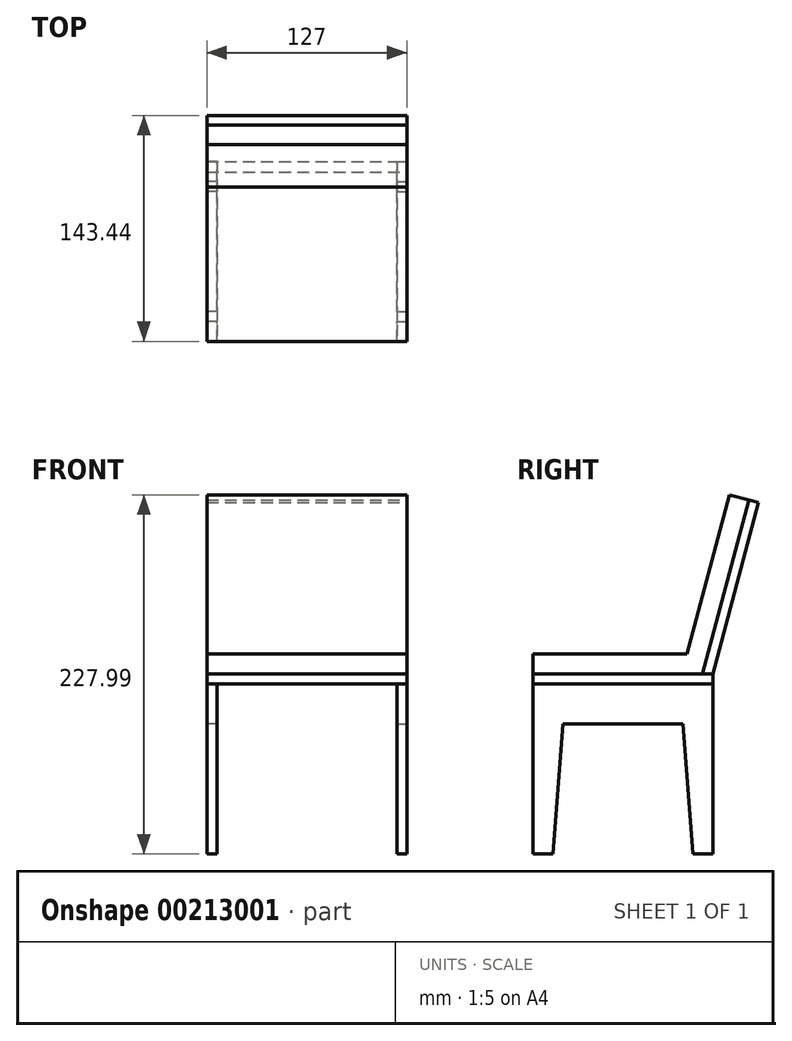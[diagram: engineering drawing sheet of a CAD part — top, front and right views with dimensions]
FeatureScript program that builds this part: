
annotation { "Feature Type Name" : "Feature", "Feature Type Description" : "" }
export const myFeature = defineFeature(function(context is Context, id is Id, definition is map)
    precondition{}
    {
        {
            var Q0;
            Q0=qCreatedBy(makeId("Top.planeOp"),FACE);
            cPlane(context, id + "F0", {"entities" : qUnion([Q0]), "cplaneType" : CPlaneType.OFFSET, "offset" : 114.3 * mm, "width" : 152.4 * mm, "height" : 152.4 * mm});
        }
        {
            var Q0;
            Q0=qCreatedBy(id+"F0.planeOp",FACE);
            var sketch = newSketch(context, id + "F1", { "sketchPlane" : qUnion([Q0])});
            skLineSegment(sketch, "E0.bottom", {"start": v(63.5, 57.15) * mm, "end": v(-63.5, 57.15) * mm});
            skLineSegment(sketch, "E0.top", {"start": v(63.5, -57.15) * mm, "end": v(-63.5, -57.15) * mm});
            skLineSegment(sketch, "E0.left", {"start": v(63.5, 57.15) * mm, "end": v(63.5, -57.15) * mm});
            skLineSegment(sketch, "E0.right", {"start": v(-63.5, 57.15) * mm, "end": v(-63.5, -57.15) * mm});
            skPoint(sketch, "E0.middle", {"position": v(0, 0) * mm});
            skSolve(sketch);
        }
        {
            var Q0;
            Q0=makeQuery(id+"F1.imprint","IMPRINT",FACE,{"disambiguationData":[TD([[makeQuery(id+"F1.imprint","IMPRINT",EDGE,{"derivedFrom":sQuery(id+"F1.wireOp",EDGE,"E0.bottom")}),1.0]])]});
            extrude(context, id + "F2", {"entities" : qUnion([Q0]), "oppositeDirection" : true, "depth" : 6.35 * mm});
        }
        {
            var Q0;
            Q0=makeQuery(id+"F2.opExtrude","SWEPT_FACE",FACE,{"disambiguationData":[OSD([sQuery(id+"F1.wireOp",EDGE,"E0.left")])]});
            var sketch = newSketch(context, id + "F3", { "sketchPlane" : qUnion([Q0])});
            skLineSegment(sketch, "E1", {"start": v(57.15, 114.3) * mm, "end": v(86.3, 223.06) * mm});
            skLineSegment(sketch, "E2", {"start": v(86.3, 223.06) * mm, "end": v(80.16, 224.7) * mm});
            skLineSegment(sketch, "E3", {"start": v(80.16, 224.7) * mm, "end": v(50.58, 114.3) * mm});
            skSolve(sketch);
        }
        {
            var Q0;
            {var subQ0=sQuery(id+"F3.wireOp",EDGE,"E1");Q0=makeQuery(id+"F3.imprint","IMPRINT",FACE,{"disambiguationData":[TD([[makeQuery(id+"F3.imprint","IMPRINT",EDGE,{"derivedFrom":subQ0}),1.0]])]});}
            var Q1;
            Q1=makeQuery(id+"F2.opExtrude","SWEPT_FACE",FACE,{"disambiguationData":[OSD([sQuery(id+"F1.wireOp",EDGE,"E0.right")])]});
            extrude(context, id + "F4", {"entities" : qUnion([Q0]), "endBound" : BoundingType.UP_TO_SURFACE, "oppositeDirection" : true, "endBoundEntityFace" : qUnion([Q1]), "depth" : 25.4 * mm});
        }
        {
            var Q0;
            Q0=makeQuery(id+"F4.opExtrude","CAP_FACE",FACE,{"disambiguationData":[OSD([sQuery(id+"F1.wireOp",EDGE,"E0.left"),sQuery(id+"F3.wireOp",EDGE,"E1"),sQuery(id+"F3.wireOp",EDGE,"E2"),sQuery(id+"F3.wireOp",EDGE,"E3")])],"isStart":true});
            var sketch = newSketch(context, id + "F5", { "sketchPlane" : qUnion([Q0])});
            skLineSegment(sketch, "E4.0", {"start": v(80.16, 224.7) * mm, "end": v(50.58, 114.3) * mm});
            skLineSegment(sketch, "E4.1", {"start": v(50.58, 114.3) * mm, "end": v(-57.15, 114.3) * mm});
            skLineSegment(sketch, "E5.0", {"start": v(40.83, 127) * mm, "end": v(-57.15, 127) * mm});
            skLineSegment(sketch, "E5.1", {"start": v(67.9, 228) * mm, "end": v(40.83, 127) * mm});
            skLineSegment(sketch, "E6", {"start": v(67.9, 228) * mm, "end": v(80.16, 224.7) * mm});
            skLineSegment(sketch, "E7", {"start": v(-57.15, 127) * mm, "end": v(-57.15, 114.3) * mm});
            skSolve(sketch);
        }
        {
            var Q0;
            Q0=makeQuery(id+"F5.imprint","IMPRINT",FACE,{"disambiguationData":[TD([[makeQuery(id+"F5.imprint","IMPRINT",EDGE,{"derivedFrom":sQuery(id+"F5.wireOp",EDGE,"E4.0")}),-1.0]])]});
            var Q1;
            Q1=makeQuery(id+"F2.opExtrude","SWEPT_FACE",FACE,{"disambiguationData":[OSD([sQuery(id+"F1.wireOp",EDGE,"E0.right")])]});
            extrude(context, id + "F6", {"entities" : qUnion([Q0]), "endBound" : BoundingType.UP_TO_SURFACE, "oppositeDirection" : true, "endBoundEntityFace" : qUnion([Q1]), "depth" : 25.4 * mm});
        }
        {
            var Q0;
            Q0=makeQuery(id+"F2.opExtrude","SWEPT_FACE",FACE,{"disambiguationData":[OSD([sQuery(id+"F1.wireOp",EDGE,"E0.left")])]});
            var sketch = newSketch(context, id + "F7", { "sketchPlane" : qUnion([Q0])});
            skLineSegment(sketch, "E8", {"start": v(-57.15, 107.95) * mm, "end": v(-57.15, 0) * mm});
            skLineSegment(sketch, "E9", {"start": v(-57.15, 0) * mm, "end": v(-44.45, 0) * mm});
            skLineSegment(sketch, "E10", {"start": v(-38.1, 82.55) * mm, "end": v(38.1, 82.55) * mm});
            skLineSegment(sketch, "E11", {"start": v(38.1, 82.55) * mm, "end": v(44.45, 0) * mm});
            skLineSegment(sketch, "E12", {"start": v(44.45, 0) * mm, "end": v(57.15, 0) * mm});
            skLineSegment(sketch, "E13", {"start": v(57.15, 0) * mm, "end": v(57.15, 107.95) * mm});
            skLineSegment(sketch, "E14", {"start": v(-38.1, 82.55) * mm, "end": v(-44.45, 0) * mm});
            skSolve(sketch);
        }
        {
            var Q0;
            Q0=makeQuery(id+"F7.imprint","IMPRINT",FACE,{"disambiguationData":[TD([[makeQuery(id+"F7.imprint","IMPRINT",EDGE,{"derivedFrom":sQuery(id+"F7.wireOp",EDGE,"E8")}),1.0]])]});
            extrude(context, id + "F8", {"entities" : qUnion([Q0]), "oppositeDirection" : true, "depth" : 6.35 * mm});
        }
        {
            var Q0;
            Q0=makeQuery(id+"F8.opExtrude","SWEPT_BODY",BODY,{"disambiguationData":[OSD([sQuery(id+"F1.wireOp",EDGE,"E0.left"),sQuery(id+"F7.wireOp",EDGE,"E8"),sQuery(id+"F7.wireOp",EDGE,"E9"),sQuery(id+"F7.wireOp",EDGE,"E10"),sQuery(id+"F7.wireOp",EDGE,"E11"),sQuery(id+"F7.wireOp",EDGE,"E12"),sQuery(id+"F7.wireOp",EDGE,"E13"),sQuery(id+"F7.wireOp",EDGE,"E14")])]});
            var Q1;
            Q1=qCreatedBy(makeId("Right.planeOp"),FACE);
            mirror(context, id + "F9", {"entities" : qUnion([Q0]), "mirrorPlane" : qUnion([Q1])});
        }
    });
